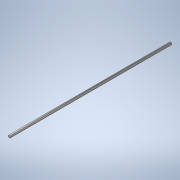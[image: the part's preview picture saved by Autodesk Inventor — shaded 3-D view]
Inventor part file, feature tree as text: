
AUTODESK INVENTOR PART (.ipt)
format: ipt  version: 2020 (Build 240168000, 168)  size: 110,592 bytes
history: native  units: in
note: dims shown in document units (in); Inventor stores cm internally (conversion verified against a paired STEP export)
features: extrude x1, sketch x1
ambient origin geometry x8: Origin, YZ Plane, XZ Plane, XY Plane, X Axis, Y Axis, Z Axis, Center Point
bodies: Solid1 (feature_tree)
feature tree (2):
  extrude  "Extrusion1"  Depth=38.0in TaperAngle=0.0deg
  sketch  "Sketch1"  dims[d0=0.5in d1=38.0in d2=0.0in]
